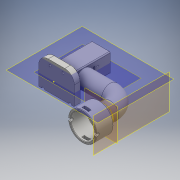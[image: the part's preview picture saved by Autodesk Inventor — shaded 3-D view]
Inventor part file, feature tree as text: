
AUTODESK INVENTOR PART (.ipt)
format: ipt  version: 2016 (Build 200138000, 138)  size: 443,904 bytes
history: native  units: mm
features: sketch x20, extrude x16, other x8, fillet x7, loft x2, projected_geometry x2, sweep x1
ambient origin geometry x8: Origin, YZ Plane, XZ Plane, XY Plane, X Axis, Y Axis, Z Axis, Center Point
bodies: Body1 (feature_tree)
feature tree (56):
  other  "ソリッド1"
  extrude  "押し出し1"  Depth=13.0mm TaperAngle=0.0deg
  fillet  "フィレット1"  Radius=1.0mm
  fillet  "フィレット2"  Radius=1.0mm
  sketch  "スケッチ2"
  extrude  "押し出し2"  Depth=10.0mm
  extrude  "押し出し3"  Depth=10.0mm
  sketch  "スケッチ3"
  extrude  "押し出し4"  Depth=4.0mm TaperAngle=0.0deg
  extrude  "押し出し5"  Depth=4.0mm TaperAngle=0.0deg
  extrude  "押し出し6"  Depth=13.0mm
  extrude  "押し出し7"  Depth=13.0mm
  fillet  "フィレット3"  Radius=7.0mm
  extrude  "押し出し8"  Depth=7.0mm TaperAngle=0.0deg
  extrude  "押し出し9"  Depth=40.0mm
  sketch  "スケッチ9"
  other  "作業平面1"
  sweep  "スイープ1"
  extrude  "押し出し10"  Depth=5.0mm
  sketch  "スケッチ12"
  other  "作業平面2"
  loft  "ロフト1"
  other  "作業平面3"
  loft  "ロフト2"
  extrude  "押し出し11"  Depth=36.0mm
  extrude  "押し出し12"  Depth=25.0mm
  fillet  "フィレット4"  Radius=55.0mm
  fillet  "フィレット5"  Radius=20.0mm
  other  "作業平面4"
  extrude  "押し出し13"  Depth=2.0mm
  other  "作業平面5"
  extrude  "押し出し14"  Depth=3.0mm
  extrude  "押し出し15"  Depth=3.0mm
  fillet  "フィレット6"  Radius=3.0mm
  fillet  "フィレット7"  Radius=3.0mm
  extrude  "押し出し20"  Depth=2.0mm
  sketch  "スケッチ1"
  sketch  "スケッチ4"
  sketch  "スケッチ5"
  sketch  "スケッチ6"
  sketch  "スケッチ7"
  sketch  "スケッチ10"
  sketch  "スケッチ11"
  projected_geometry  "投影ループ1"
  sketch  "スケッチ13"
  other  "エッジ1"
  sketch  "スケッチ15"
  sketch  "スケッチ18"
  sketch  "スケッチ19"
  sketch  "スケッチ20"
  projected_geometry  "投影ループ2"
  sketch  "スケッチ21"
  sketch  "スケッチ22"
  sketch  "スケッチ23"
  sketch  "スケッチ27"
  other  "断面エッジを投影1"
